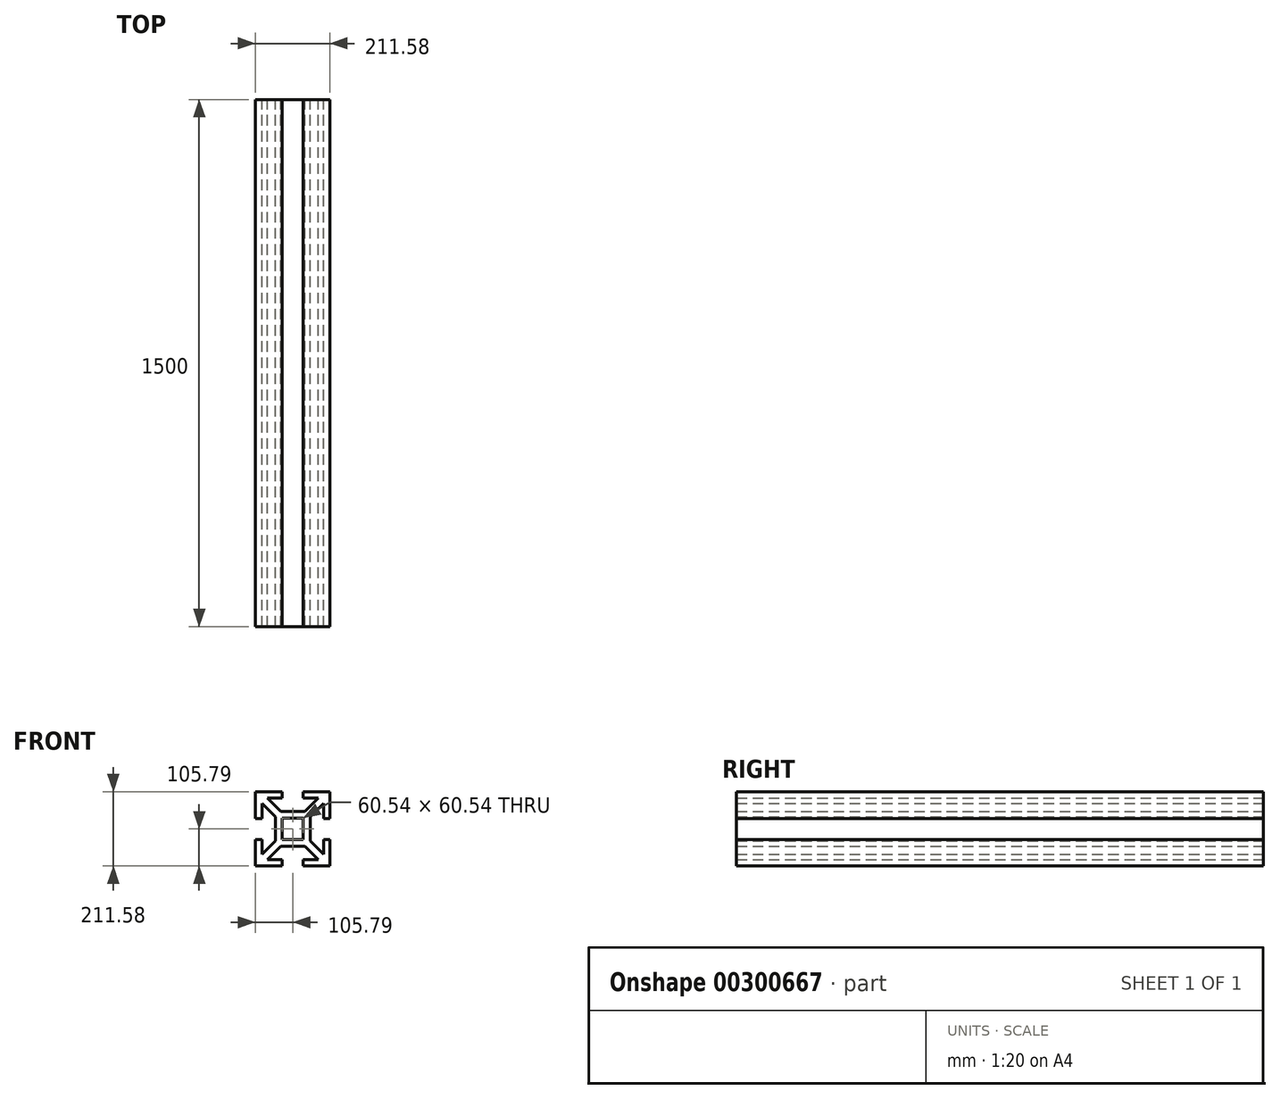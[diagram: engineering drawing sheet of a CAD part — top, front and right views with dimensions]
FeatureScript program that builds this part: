
annotation { "Feature Type Name" : "Feature", "Feature Type Description" : "" }
export const myFeature = defineFeature(function(context is Context, id is Id, definition is map)
    precondition{}
    {
        {
            var Q0;
            Q0=qCreatedBy(makeId("Front.planeOp"),FACE);
            var sketch = newSketch(context, id + "F0", { "sketchPlane" : qUnion([Q0])});
            skLineSegment(sketch, "E0", {"start": v(0, 0) * mm, "end": v(105.79, 105.79) * mm, "construction": true});
            skLineSegment(sketch, "E1", {"start": v(0, 49.56) * mm, "end": v(34.3, 49.56) * mm});
            skLineSegment(sketch, "E2", {"start": v(34.3, 49.56) * mm, "end": v(72.43, 87.68) * mm});
            skLineSegment(sketch, "E3", {"start": v(72.43, 87.68) * mm, "end": v(29.86, 87.68) * mm});
            skLineSegment(sketch, "E4", {"start": v(29.86, 87.68) * mm, "end": v(29.86, 105.79) * mm});
            skLineSegment(sketch, "E5", {"start": v(29.86, 105.79) * mm, "end": v(105.79, 105.79) * mm});
            skLineSegment(sketch, "E6", {"start": v(0, 30.27) * mm, "end": v(30.27, 30.27) * mm});
            skLineSegment(sketch, "E7.MirrorCS", {"start": v(49.56, 0) * mm, "end": v(49.56, 34.3) * mm});
            skLineSegment(sketch, "E8.MirrorCS", {"start": v(30.27, 0) * mm, "end": v(30.27, 30.27) * mm});
            skLineSegment(sketch, "E9.MirrorCS", {"start": v(49.56, 34.3) * mm, "end": v(87.68, 72.43) * mm});
            skLineSegment(sketch, "E10.MirrorCS", {"start": v(87.68, 29.86) * mm, "end": v(105.79, 29.86) * mm});
            skLineSegment(sketch, "E11.MirrorCS", {"start": v(87.68, 72.43) * mm, "end": v(87.68, 29.86) * mm});
            skLineSegment(sketch, "E12.MirrorCS", {"start": v(105.79, 29.86) * mm, "end": v(105.79, 105.79) * mm});
            skLineSegment(sketch, "E13.MirrorCS", {"start": v(87.68, -29.86) * mm, "end": v(105.79, -29.86) * mm});
            skLineSegment(sketch, "E14.MirrorCS", {"start": v(105.79, -29.86) * mm, "end": v(105.79, -105.79) * mm});
            skLineSegment(sketch, "E15.MirrorCS", {"start": v(87.68, -72.43) * mm, "end": v(87.68, -29.86) * mm});
            skLineSegment(sketch, "E16.MirrorCS", {"start": v(49.56, -34.3) * mm, "end": v(87.68, -72.43) * mm});
            skLineSegment(sketch, "E17.MirrorCS", {"start": v(30.27, 0) * mm, "end": v(30.27, -30.27) * mm});
            skLineSegment(sketch, "E18.MirrorCS", {"start": v(49.56, 0) * mm, "end": v(49.56, -34.3) * mm});
            skLineSegment(sketch, "E19.MirrorCS", {"start": v(0, -30.27) * mm, "end": v(30.27, -30.27) * mm});
            skLineSegment(sketch, "E20.MirrorCS", {"start": v(34.3, -49.56) * mm, "end": v(72.43, -87.68) * mm});
            skLineSegment(sketch, "E21.MirrorCS", {"start": v(0, -49.56) * mm, "end": v(34.3, -49.56) * mm});
            skLineSegment(sketch, "E22.MirrorCS", {"start": v(29.86, -105.79) * mm, "end": v(105.79, -105.79) * mm});
            skLineSegment(sketch, "E23.MirrorCS", {"start": v(29.86, -87.68) * mm, "end": v(29.86, -105.79) * mm});
            skLineSegment(sketch, "E24.MirrorCS", {"start": v(72.43, -87.68) * mm, "end": v(29.86, -87.68) * mm});
            skLineSegment(sketch, "E25.MirrorCS", {"start": v(0, 0) * mm, "end": v(105.79, -105.79) * mm, "construction": true});
            skLineSegment(sketch, "E26.MirrorCS", {"start": v(-87.68, 29.86) * mm, "end": v(-105.79, 29.86) * mm});
            skLineSegment(sketch, "E27.MirrorCS", {"start": v(-49.56, -34.3) * mm, "end": v(-87.68, -72.43) * mm});
            skLineSegment(sketch, "E28.MirrorCS", {"start": v(-49.56, 0) * mm, "end": v(-49.56, -34.3) * mm});
            skLineSegment(sketch, "E29.MirrorCS", {"start": v(-34.3, -49.56) * mm, "end": v(-72.43, -87.68) * mm});
            skLineSegment(sketch, "E30.MirrorCS", {"start": v(-29.86, -105.79) * mm, "end": v(-105.79, -105.79) * mm});
            skLineSegment(sketch, "E31.MirrorCS", {"start": v(-29.86, -87.68) * mm, "end": v(-29.86, -105.79) * mm});
            skLineSegment(sketch, "E32.MirrorCS", {"start": v(0, 0) * mm, "end": v(-105.79, -105.79) * mm, "construction": true});
            skLineSegment(sketch, "E33.MirrorCS", {"start": v(-105.79, 29.86) * mm, "end": v(-105.79, 105.79) * mm});
            skLineSegment(sketch, "E34.MirrorCS", {"start": v(-87.68, 72.43) * mm, "end": v(-87.68, 29.86) * mm});
            skLineSegment(sketch, "E35.MirrorCS", {"start": v(-49.56, 34.3) * mm, "end": v(-87.68, 72.43) * mm});
            skLineSegment(sketch, "E36.MirrorCS", {"start": v(-30.27, 0) * mm, "end": v(-30.27, 30.27) * mm});
            skLineSegment(sketch, "E37.MirrorCS", {"start": v(-49.56, 0) * mm, "end": v(-49.56, 34.3) * mm});
            skLineSegment(sketch, "E38.MirrorCS", {"start": v(0, 30.27) * mm, "end": v(-30.27, 30.27) * mm});
            skLineSegment(sketch, "E39.MirrorCS", {"start": v(-29.86, 105.79) * mm, "end": v(-105.79, 105.79) * mm});
            skLineSegment(sketch, "E40.MirrorCS", {"start": v(-29.86, 87.68) * mm, "end": v(-29.86, 105.79) * mm});
            skLineSegment(sketch, "E41.MirrorCS", {"start": v(-72.43, 87.68) * mm, "end": v(-29.86, 87.68) * mm});
            skLineSegment(sketch, "E42.MirrorCS", {"start": v(0, 49.56) * mm, "end": v(-34.3, 49.56) * mm});
            skLineSegment(sketch, "E43.MirrorCS", {"start": v(-72.43, -87.68) * mm, "end": v(-29.86, -87.68) * mm});
            skLineSegment(sketch, "E44.MirrorCS", {"start": v(0, -49.56) * mm, "end": v(-34.3, -49.56) * mm});
            skLineSegment(sketch, "E45.MirrorCS", {"start": v(0, -30.27) * mm, "end": v(-30.27, -30.27) * mm});
            skLineSegment(sketch, "E46.MirrorCS", {"start": v(-87.68, -72.43) * mm, "end": v(-87.68, -29.86) * mm});
            skLineSegment(sketch, "E47.MirrorCS", {"start": v(-34.3, 49.56) * mm, "end": v(-72.43, 87.68) * mm});
            skLineSegment(sketch, "E48.MirrorCS", {"start": v(-30.27, 0) * mm, "end": v(-30.27, -30.27) * mm});
            skLineSegment(sketch, "E49.MirrorCS", {"start": v(-87.68, -29.86) * mm, "end": v(-105.79, -29.86) * mm});
            skLineSegment(sketch, "E50.MirrorCS", {"start": v(0, 0) * mm, "end": v(-105.79, 105.79) * mm, "construction": true});
            skLineSegment(sketch, "E51.MirrorCS", {"start": v(-105.79, -29.86) * mm, "end": v(-105.79, -105.79) * mm});
            skSolve(sketch);
        }
        {
            var Q0;
            Q0=makeQuery(id+"F0.imprint","IMPRINT",FACE,{"disambiguationData":[TD([[makeQuery(id+"F0.imprint","IMPRINT",EDGE,{"derivedFrom":sQuery(id+"F0.wireOp",EDGE,"E1")}),-1.0]])]});
            extrude(context, id + "F1", {"entities" : qUnion([Q0]), "depth" : 1500 * mm});
        }
    });
